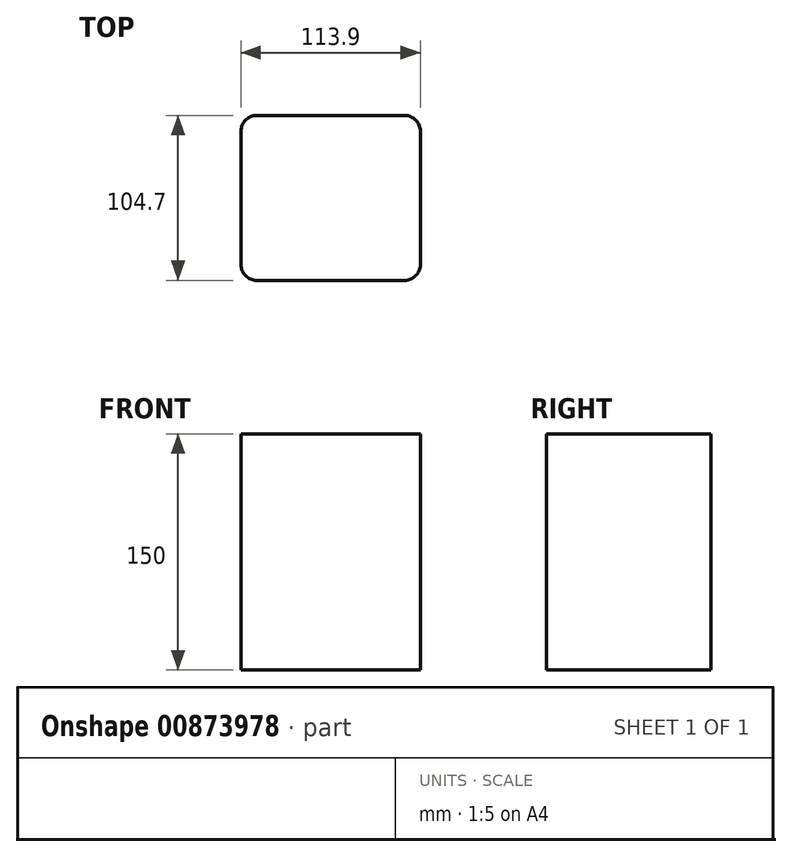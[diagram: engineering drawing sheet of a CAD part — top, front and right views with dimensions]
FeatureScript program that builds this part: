
annotation { "Feature Type Name" : "Feature", "Feature Type Description" : "" }
export const myFeature = defineFeature(function(context is Context, id is Id, definition is map)
    precondition{}
    {
        {
            var Q0;
            Q0=qCreatedBy(makeId("Top.planeOp"),FACE);
            var sketch = newSketch(context, id + "F0", { "sketchPlane" : qUnion([Q0])});
            skLineSegment(sketch, "E0.bottom", {"start": v(46.95, -52.35) * mm, "end": v(-46.95, -52.35) * mm});
            skLineSegment(sketch, "E0.top", {"start": v(46.95, 52.35) * mm, "end": v(-46.95, 52.35) * mm});
            skLineSegment(sketch, "E0.left", {"start": v(56.95, -42.35) * mm, "end": v(56.95, 42.35) * mm});
            skLineSegment(sketch, "E0.right", {"start": v(-56.95, -42.35) * mm, "end": v(-56.95, 42.35) * mm});
            skPoint(sketch, "E0.middle", {"position": v(0, 0) * mm});
            skPoint(sketch, "E1.visualSharp", {"position": v(56.95, 52.35) * mm});
            skArc(sketch, "E2.filletArc", {"start": v(56.95, 42.35) * mm, "mid": v(54.02, 49.43) * mm, "end": v(46.95, 52.35) * mm});
            skPoint(sketch, "E3.visualSharp", {"position": v(56.95, -52.35) * mm});
            skArc(sketch, "E3.filletArc", {"start": v(46.95, -52.35) * mm, "mid": v(54.02, -49.43) * mm, "end": v(56.95, -42.35) * mm});
            skPoint(sketch, "E4.visualSharp", {"position": v(-56.95, -52.35) * mm});
            skArc(sketch, "E4.filletArc", {"start": v(-56.95, -42.35) * mm, "mid": v(-54.02, -49.43) * mm, "end": v(-46.95, -52.35) * mm});
            skPoint(sketch, "E5.visualSharp", {"position": v(-56.95, 52.35) * mm});
            skArc(sketch, "E5.filletArc", {"start": v(-46.95, 52.35) * mm, "mid": v(-54.02, 49.43) * mm, "end": v(-56.95, 42.35) * mm});
            skSolve(sketch);
        }
        {
            var Q0;
            Q0 = qSketchRegion(id + "F0", true);
            extrude(context, id + "F1", {"entities" : qUnion([Q0]), "depth" : 150 * mm, "offsetDistance" : 25.4 * mm});
        }
    });
